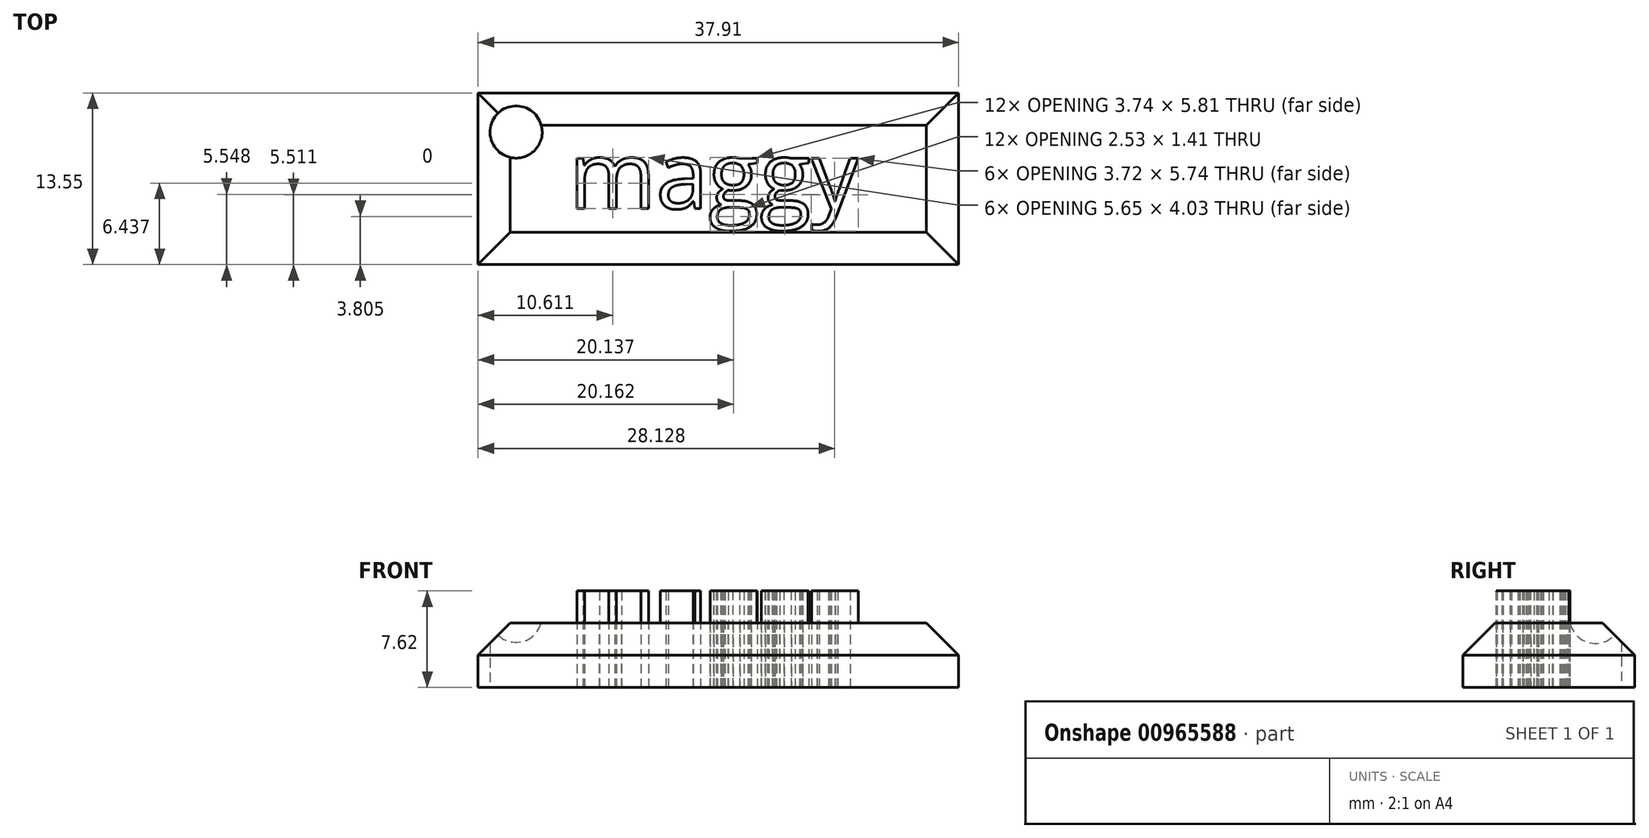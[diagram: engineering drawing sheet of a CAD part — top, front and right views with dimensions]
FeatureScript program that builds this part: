
annotation { "Feature Type Name" : "Feature", "Feature Type Description" : "" }
export const myFeature = defineFeature(function(context is Context, id is Id, definition is map)
    precondition{}
    {
        {
            var Q0;
            Q0=qCreatedBy(makeId("Top.planeOp"),FACE);
            var sketch = newSketch(context, id + "F0", { "sketchPlane" : qUnion([Q0])});
            skLineSegment(sketch, "E0.bottom", {"start": v(-64.63, 27.71) * mm, "end": v(-26.72, 27.71) * mm});
            skLineSegment(sketch, "E0.top", {"start": v(-64.63, 41.26) * mm, "end": v(-26.72, 41.26) * mm});
            skLineSegment(sketch, "E0.left", {"start": v(-64.63, 27.71) * mm, "end": v(-64.63, 41.26) * mm});
            skLineSegment(sketch, "E0.right", {"start": v(-26.72, 27.71) * mm, "end": v(-26.72, 41.26) * mm});
            skText(sketch, "E1", { "text": "maggy", "fontName": "OpenSans-Regular.ttf"});
            skCircle(sketch, "E2", {"center": v(-61.64, 38.18) * mm, "radius": 2.06 * mm});
            const initialGuessF0  = {"E1": [-0.05748, 0.03213, 1, 0, 0.00533]};
            skSetInitialGuess(sketch, initialGuessF0);
            skSolve(sketch);
        }
        {
            var Q0;
            Q0=makeQuery(id+"F0.imprint","IMPRINT",FACE,{"disambiguationData":[TD([[makeQuery(id+"F0.imprint","IMPRINT",EDGE,{"derivedFrom":sQuery(id+"F0.wireOp",EDGE,"E1.sketch_text.stroke-93")}),1.0]])]});
            var Q1;
            Q1=makeQuery(id+"F0.imprint","IMPRINT",FACE,{"disambiguationData":[TD([[makeQuery(id+"F0.imprint","IMPRINT",EDGE,{"derivedFrom":sQuery(id+"F0.wireOp",EDGE,"E1.sketch_text.stroke-137")}),1.0]])]});
            var Q2;
            Q2=makeQuery(id+"F0.imprint","IMPRINT",FACE,{"disambiguationData":[TD([[makeQuery(id+"F0.imprint","IMPRINT",EDGE,{"derivedFrom":sQuery(id+"F0.wireOp",EDGE,"E1.sketch_text.stroke-128")}),1.0]])]});
            var Q3;
            Q3=makeQuery(id+"F0.imprint","IMPRINT",FACE,{"disambiguationData":[TD([[makeQuery(id+"F0.imprint","IMPRINT",EDGE,{"derivedFrom":sQuery(id+"F0.wireOp",EDGE,"E1.sketch_text.stroke-84")}),1.0]])]});
            var Q4;
            Q4=makeQuery(id+"F0.imprint","IMPRINT",FACE,{"disambiguationData":[TD([[makeQuery(id+"F0.imprint","IMPRINT",EDGE,{"derivedFrom":sQuery(id+"F0.wireOp",EDGE,"E1.sketch_text.stroke-47")}),1.0]])]});
            var Q5;
            Q5=makeQuery(id+"F0.imprint","IMPRINT",FACE,{"disambiguationData":[TD([[makeQuery(id+"F0.imprint","IMPRINT",EDGE,{"derivedFrom":sQuery(id+"F0.wireOp",EDGE,"E0.bottom")}),1.0]])]});
            extrude(context, id + "F1", {"entities" : qUnion([Q0, Q1, Q2, Q3, Q4, Q5]), "depth" : 5.08 * mm, "offsetDistance" : 25.4 * mm});
        }
        {
            var Q0;
            Q0=makeQuery(id+"F0.imprint","IMPRINT",FACE,{"disambiguationData":[TD([[makeQuery(id+"F0.imprint","IMPRINT",EDGE,{"derivedFrom":sQuery(id+"F0.wireOp",EDGE,"E1.sketch_text.stroke-0")}),-1.0]])]});
            var Q1;
            Q1=makeQuery(id+"F0.imprint","IMPRINT",FACE,{"disambiguationData":[TD([[makeQuery(id+"F0.imprint","IMPRINT",EDGE,{"derivedFrom":sQuery(id+"F0.wireOp",EDGE,"E1.sketch_text.stroke-28")}),-1.0]])]});
            var Q2;
            Q2=makeQuery(id+"F0.imprint","IMPRINT",FACE,{"disambiguationData":[TD([[makeQuery(id+"F0.imprint","IMPRINT",EDGE,{"derivedFrom":sQuery(id+"F0.wireOp",EDGE,"E1.sketch_text.stroke-55")}),-1.0]])]});
            var Q3;
            Q3=makeQuery(id+"F0.imprint","IMPRINT",FACE,{"disambiguationData":[TD([[makeQuery(id+"F0.imprint","IMPRINT",EDGE,{"derivedFrom":sQuery(id+"F0.wireOp",EDGE,"E1.sketch_text.stroke-99")}),-1.0]])]});
            var Q4;
            Q4=makeQuery(id+"F0.imprint","IMPRINT",FACE,{"disambiguationData":[TD([[makeQuery(id+"F0.imprint","IMPRINT",EDGE,{"derivedFrom":sQuery(id+"F0.wireOp",EDGE,"E1.sketch_text.stroke-143")}),-1.0]])]});
            extrude(context, id + "F2", {"entities" : qUnion([Q0, Q1, Q2, Q3, Q4]), "depth" : 7.62 * mm, "offsetDistance" : 25.4 * mm});
        }
        {
            var Q0;
            Q0=makeQuery(id+"F1.opExtrude","CAP_EDGE",EDGE,{"disambiguationData":[OSD([sQuery(id+"F0.wireOp",EDGE,"E0.right")])],"isStart":false});
            var Q1;
            Q1=makeQuery(id+"F1.opExtrude","CAP_EDGE",EDGE,{"disambiguationData":[OSD([sQuery(id+"F0.wireOp",EDGE,"E0.bottom")])],"isStart":false});
            var Q2;
            Q2=makeQuery(id+"F1.opExtrude","CAP_EDGE",EDGE,{"disambiguationData":[OSD([sQuery(id+"F0.wireOp",EDGE,"E0.top")])],"isStart":false});
            var Q3;
            Q3=makeQuery(id+"F1.opExtrude","CAP_EDGE",EDGE,{"disambiguationData":[OSD([sQuery(id+"F0.wireOp",EDGE,"E0.left")])],"isStart":false});
            chamfer(context, id + "F3", {"entities" : qUnion([Q0, Q1, Q2, Q3]), "width" : 2.54 * mm, "tangentPropagation" : true});
        }
    });
